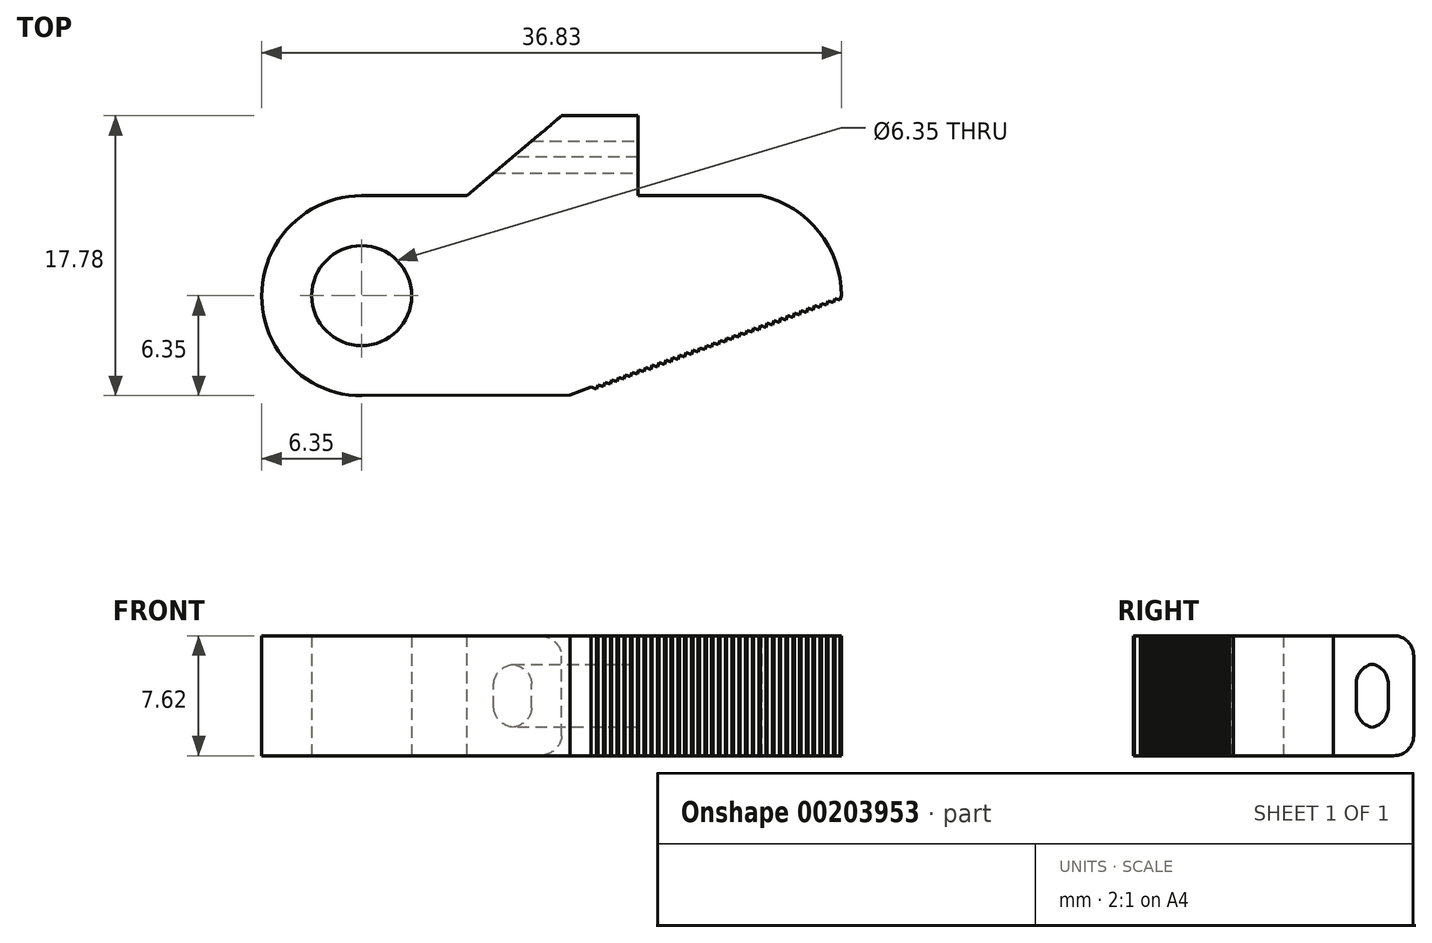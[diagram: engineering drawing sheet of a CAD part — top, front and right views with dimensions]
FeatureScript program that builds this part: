
annotation { "Feature Type Name" : "Feature", "Feature Type Description" : "" }
export const myFeature = defineFeature(function(context is Context, id is Id, definition is map)
    precondition{}
    {
        {
            var Q0;
            Q0=qCreatedBy(makeId("Top.planeOp"),FACE);
            var sketch = newSketch(context, id + "F0", { "sketchPlane" : qUnion([Q0])});
            skCircle(sketch, "E0", {"center": v(0, 0) * mm, "radius": 3.18 * mm});
            skCircle(sketch, "E1", {"center": v(0, 0) * mm, "radius": 6.35 * mm});
            skLineSegment(sketch, "E2", {"start": v(0, 0) * mm, "end": v(30.48, 0) * mm});
            skLineSegment(sketch, "E3", {"start": v(0, 0) * mm, "end": v(25.4, 0) * mm});
            skLineSegment(sketch, "E4", {"start": v(25.4, 0) * mm, "end": v(25.4, 6.35) * mm});
            skLineSegment(sketch, "E5", {"start": v(25.4, 0) * mm, "end": v(25.4, -6.35) * mm});
            skArc(sketch, "E6", {"start": v(30.48, 0) * mm, "mid": v(29.04, 4.06) * mm, "end": v(25.4, 6.35) * mm});
            skLineSegment(sketch, "E7", {"start": v(30.48, 0) * mm, "end": v(13.24, -6.3) * mm});
            skLineSegment(sketch, "E8", {"start": v(13.24, -6.3) * mm, "end": v(0, -6.35) * mm});
            skLineSegment(sketch, "E9", {"start": v(25.4, 6.35) * mm, "end": v(0, 6.35) * mm});
            skLineSegment(sketch, "E10", {"start": v(30.48, 0) * mm, "end": v(30.39, -0.28) * mm});
            skLineSegment(sketch, "E11", {"start": v(30.39, -0.28) * mm, "end": v(30.03, -0.16) * mm});
            skLineSegment(sketch, "E12.1.0.0", {"start": v(29.96, -0.44) * mm, "end": v(29.6, -0.32) * mm});
            skLineSegment(sketch, "E12.1.0.1", {"start": v(30.05, -0.16) * mm, "end": v(29.96, -0.44) * mm});
            skLineSegment(sketch, "E12.2.0.0", {"start": v(29.53, -0.6) * mm, "end": v(29.18, -0.48) * mm});
            skLineSegment(sketch, "E12.2.0.1", {"start": v(29.62, -0.31) * mm, "end": v(29.53, -0.6) * mm});
            skLineSegment(sketch, "E12.3.0.0", {"start": v(29.1, -0.75) * mm, "end": v(28.75, -0.63) * mm});
            skLineSegment(sketch, "E12.3.0.1", {"start": v(29.2, -0.47) * mm, "end": v(29.1, -0.75) * mm});
            skLineSegment(sketch, "E12.4.0.0", {"start": v(28.67, -0.9) * mm, "end": v(28.32, -0.8) * mm});
            skLineSegment(sketch, "E12.4.0.1", {"start": v(28.76, -0.63) * mm, "end": v(28.67, -0.9) * mm});
            skLineSegment(sketch, "E12.5.0.0", {"start": v(28.24, -1.06) * mm, "end": v(27.89, -0.95) * mm});
            skLineSegment(sketch, "E12.5.0.1", {"start": v(28.33, -0.79) * mm, "end": v(28.24, -1.06) * mm});
            skLineSegment(sketch, "E12.6.0.0", {"start": v(27.81, -1.22) * mm, "end": v(27.46, -1.1) * mm});
            skLineSegment(sketch, "E12.6.0.1", {"start": v(27.9, -0.94) * mm, "end": v(27.81, -1.22) * mm});
            skLineSegment(sketch, "E12.7.0.0", {"start": v(27.38, -1.38) * mm, "end": v(27.03, -1.26) * mm});
            skLineSegment(sketch, "E12.7.0.1", {"start": v(27.47, -1.1) * mm, "end": v(27.38, -1.38) * mm});
            skLineSegment(sketch, "E12.8.0.0", {"start": v(26.95, -1.54) * mm, "end": v(26.6, -1.42) * mm});
            skLineSegment(sketch, "E12.8.0.1", {"start": v(27.05, -1.26) * mm, "end": v(26.95, -1.54) * mm});
            skLineSegment(sketch, "E12.9.0.0", {"start": v(26.53, -1.7) * mm, "end": v(26.17, -1.58) * mm});
            skLineSegment(sketch, "E12.9.0.1", {"start": v(26.62, -1.41) * mm, "end": v(26.53, -1.7) * mm});
            skLineSegment(sketch, "E12.direction1", {"start": v(30.03, -0.16) * mm, "end": v(29.6, -0.32) * mm, "construction": true});
            skLineSegment(sketch, "E13.1.0.0", {"start": v(26.1, -1.85) * mm, "end": v(25.74, -1.73) * mm});
            skLineSegment(sketch, "E13.1.0.1", {"start": v(26.19, -1.57) * mm, "end": v(26.1, -1.85) * mm});
            skLineSegment(sketch, "E13.2.0.0", {"start": v(25.67, -2) * mm, "end": v(25.31, -1.9) * mm});
            skLineSegment(sketch, "E13.2.0.1", {"start": v(25.76, -1.73) * mm, "end": v(25.67, -2) * mm});
            skLineSegment(sketch, "E13.3.0.0", {"start": v(25.24, -2.16) * mm, "end": v(24.88, -2.05) * mm});
            skLineSegment(sketch, "E13.3.0.1", {"start": v(25.33, -1.88) * mm, "end": v(25.24, -2.16) * mm});
            skLineSegment(sketch, "E13.4.0.0", {"start": v(24.8, -2.32) * mm, "end": v(24.45, -2.2) * mm});
            skLineSegment(sketch, "E13.4.0.1", {"start": v(24.9, -2.04) * mm, "end": v(24.8, -2.32) * mm});
            skLineSegment(sketch, "E13.5.0.0", {"start": v(24.38, -2.48) * mm, "end": v(24.02, -2.36) * mm});
            skLineSegment(sketch, "E13.5.0.1", {"start": v(24.47, -2.2) * mm, "end": v(24.38, -2.48) * mm});
            skLineSegment(sketch, "E13.6.0.0", {"start": v(23.95, -2.63) * mm, "end": v(23.6, -2.52) * mm});
            skLineSegment(sketch, "E13.6.0.1", {"start": v(24.04, -2.36) * mm, "end": v(23.95, -2.63) * mm});
            skLineSegment(sketch, "E13.7.0.0", {"start": v(23.52, -2.8) * mm, "end": v(23.16, -2.67) * mm});
            skLineSegment(sketch, "E13.7.0.1", {"start": v(23.6, -2.51) * mm, "end": v(23.52, -2.8) * mm});
            skLineSegment(sketch, "E13.8.0.0", {"start": v(23.09, -2.95) * mm, "end": v(22.73, -2.83) * mm});
            skLineSegment(sketch, "E13.8.0.1", {"start": v(23.18, -2.67) * mm, "end": v(23.09, -2.95) * mm});
            skLineSegment(sketch, "E13.9.0.0", {"start": v(22.66, -3.1) * mm, "end": v(22.3, -2.99) * mm});
            skLineSegment(sketch, "E13.9.0.1", {"start": v(22.75, -2.83) * mm, "end": v(22.66, -3.1) * mm});
            skLineSegment(sketch, "E13.direction1", {"start": v(26.17, -1.58) * mm, "end": v(25.74, -1.73) * mm, "construction": true});
            skLineSegment(sketch, "E14.1.0.0", {"start": v(22.23, -3.26) * mm, "end": v(21.88, -3.15) * mm});
            skLineSegment(sketch, "E14.1.0.1", {"start": v(22.32, -2.98) * mm, "end": v(22.23, -3.26) * mm});
            skLineSegment(sketch, "E14.2.0.0", {"start": v(21.8, -3.42) * mm, "end": v(21.45, -3.3) * mm});
            skLineSegment(sketch, "E14.2.0.1", {"start": v(21.9, -3.14) * mm, "end": v(21.8, -3.42) * mm});
            skLineSegment(sketch, "E14.3.0.0", {"start": v(21.37, -3.57) * mm, "end": v(21.02, -3.46) * mm});
            skLineSegment(sketch, "E14.3.0.1", {"start": v(21.46, -3.3) * mm, "end": v(21.37, -3.57) * mm});
            skLineSegment(sketch, "E14.4.0.0", {"start": v(20.94, -3.73) * mm, "end": v(20.59, -3.62) * mm});
            skLineSegment(sketch, "E14.4.0.1", {"start": v(21.03, -3.45) * mm, "end": v(20.94, -3.73) * mm});
            skLineSegment(sketch, "E14.5.0.0", {"start": v(20.51, -3.89) * mm, "end": v(20.16, -3.77) * mm});
            skLineSegment(sketch, "E14.5.0.1", {"start": v(20.6, -3.61) * mm, "end": v(20.51, -3.89) * mm});
            skLineSegment(sketch, "E14.6.0.0", {"start": v(20.08, -4.05) * mm, "end": v(19.73, -3.93) * mm});
            skLineSegment(sketch, "E14.6.0.1", {"start": v(20.17, -3.77) * mm, "end": v(20.08, -4.05) * mm});
            skLineSegment(sketch, "E14.7.0.0", {"start": v(19.65, -4.2) * mm, "end": v(19.3, -4.09) * mm});
            skLineSegment(sketch, "E14.7.0.1", {"start": v(19.74, -3.92) * mm, "end": v(19.65, -4.2) * mm});
            skLineSegment(sketch, "E14.8.0.0", {"start": v(19.22, -4.36) * mm, "end": v(18.87, -4.24) * mm});
            skLineSegment(sketch, "E14.8.0.1", {"start": v(19.32, -4.08) * mm, "end": v(19.22, -4.36) * mm});
            skLineSegment(sketch, "E14.9.0.0", {"start": v(18.8, -4.52) * mm, "end": v(18.44, -4.4) * mm});
            skLineSegment(sketch, "E14.9.0.1", {"start": v(18.89, -4.24) * mm, "end": v(18.8, -4.52) * mm});
            skLineSegment(sketch, "E14.direction1", {"start": v(22.3, -2.99) * mm, "end": v(21.88, -3.15) * mm, "construction": true});
            skLineSegment(sketch, "E15.1.0.0", {"start": v(18.46, -4.4) * mm, "end": v(18.37, -4.67) * mm});
            skLineSegment(sketch, "E15.1.0.1", {"start": v(18.37, -4.67) * mm, "end": v(18.01, -4.56) * mm});
            skLineSegment(sketch, "E15.2.0.0", {"start": v(18.03, -4.55) * mm, "end": v(17.94, -4.83) * mm});
            skLineSegment(sketch, "E15.2.0.1", {"start": v(17.94, -4.83) * mm, "end": v(17.58, -4.71) * mm});
            skLineSegment(sketch, "E15.3.0.0", {"start": v(17.6, -4.7) * mm, "end": v(17.5, -4.99) * mm});
            skLineSegment(sketch, "E15.3.0.1", {"start": v(17.5, -4.99) * mm, "end": v(17.15, -4.87) * mm});
            skLineSegment(sketch, "E15.4.0.0", {"start": v(17.17, -4.86) * mm, "end": v(17.08, -5.14) * mm});
            skLineSegment(sketch, "E15.4.0.1", {"start": v(17.08, -5.14) * mm, "end": v(16.72, -5.03) * mm});
            skLineSegment(sketch, "E15.5.0.0", {"start": v(16.74, -5.02) * mm, "end": v(16.65, -5.3) * mm});
            skLineSegment(sketch, "E15.5.0.1", {"start": v(16.65, -5.3) * mm, "end": v(16.3, -5.18) * mm});
            skLineSegment(sketch, "E15.6.0.0", {"start": v(16.3, -5.18) * mm, "end": v(16.22, -5.45) * mm});
            skLineSegment(sketch, "E15.6.0.1", {"start": v(16.22, -5.45) * mm, "end": v(15.86, -5.34) * mm});
            skLineSegment(sketch, "E15.7.0.0", {"start": v(15.88, -5.33) * mm, "end": v(15.79, -5.61) * mm});
            skLineSegment(sketch, "E15.7.0.1", {"start": v(15.79, -5.61) * mm, "end": v(15.43, -5.5) * mm});
            skLineSegment(sketch, "E15.8.0.0", {"start": v(15.45, -5.49) * mm, "end": v(15.36, -5.77) * mm});
            skLineSegment(sketch, "E15.8.0.1", {"start": v(15.36, -5.77) * mm, "end": v(15, -5.65) * mm});
            skLineSegment(sketch, "E15.9.0.0", {"start": v(15.02, -5.65) * mm, "end": v(14.93, -5.92) * mm});
            skLineSegment(sketch, "E15.9.0.1", {"start": v(14.93, -5.92) * mm, "end": v(14.57, -5.8) * mm});
            skLineSegment(sketch, "E15.direction1", {"start": v(18.8, -4.52) * mm, "end": v(18.37, -4.67) * mm, "construction": true});
            skLineSegment(sketch, "E16", {"start": v(14.57, -5.8) * mm, "end": v(29.04, 0.72) * mm});
            skLineSegment(sketch, "E17", {"start": v(29.04, 0.72) * mm, "end": v(30.48, 0) * mm});
            skSolve(sketch);
        }
        {
            var Q0;
            Q0 = qSketchRegion(id + "F0", true);
            var Q1;
            {var subQ1=sQuery(id+"F0.wireOp",EDGE,"E2");var subQ3=sQuery(id+"F0.wireOp",EDGE,"E16");var subQ4=makeQuery(id+"F0.imprint","INTERSECT",VERTEX,{"derivedFrom":[subQ1,subQ3]});Q1=makeQuery(id+"F0.imprint","IMPRINT",FACE,{"disambiguationData":[TD([[makeQuery(id+"F0.imprint","IMPRINT",EDGE,{"disambiguationData":[TD([[subQ4,1.0]])],"derivedFrom":subQ3}),1.0]])]});}
            extrude(context, id + "F1", {"entities" : qUnion([Q0, Q1]), "depth" : 7.62 * mm});
        }
        {
            var Q0;
            Q0=makeQuery(id+"F1.opExtrude","CAP_FACE",FACE,{"disambiguationData":[OSD([sQuery(id+"F0.wireOp",EDGE,"E0"),sQuery(id+"F0.wireOp",EDGE,"E1"),sQuery(id+"F0.wireOp",EDGE,"E6"),sQuery(id+"F0.wireOp",EDGE,"E7"),sQuery(id+"F0.wireOp",EDGE,"E8"),sQuery(id+"F0.wireOp",EDGE,"E9"),sQuery(id+"F0.wireOp",EDGE,"E10"),sQuery(id+"F0.wireOp",EDGE,"E11"),sQuery(id+"F0.wireOp",EDGE,"E12.1.0.0"),sQuery(id+"F0.wireOp",EDGE,"E12.1.0.1"),sQuery(id+"F0.wireOp",EDGE,"E12.2.0.0"),sQuery(id+"F0.wireOp",EDGE,"E12.2.0.1"),sQuery(id+"F0.wireOp",EDGE,"E12.3.0.0"),sQuery(id+"F0.wireOp",EDGE,"E12.3.0.1"),sQuery(id+"F0.wireOp",EDGE,"E12.4.0.0"),sQuery(id+"F0.wireOp",EDGE,"E12.4.0.1"),sQuery(id+"F0.wireOp",EDGE,"E12.5.0.0"),sQuery(id+"F0.wireOp",EDGE,"E12.5.0.1"),sQuery(id+"F0.wireOp",EDGE,"E12.6.0.0"),sQuery(id+"F0.wireOp",EDGE,"E12.6.0.1"),sQuery(id+"F0.wireOp",EDGE,"E12.7.0.0"),sQuery(id+"F0.wireOp",EDGE,"E12.7.0.1"),sQuery(id+"F0.wireOp",EDGE,"E12.8.0.0"),sQuery(id+"F0.wireOp",EDGE,"E12.8.0.1"),sQuery(id+"F0.wireOp",EDGE,"E12.9.0.0"),sQuery(id+"F0.wireOp",EDGE,"E12.9.0.1"),sQuery(id+"F0.wireOp",EDGE,"E13.1.0.0"),sQuery(id+"F0.wireOp",EDGE,"E13.1.0.1"),sQuery(id+"F0.wireOp",EDGE,"E13.2.0.0"),sQuery(id+"F0.wireOp",EDGE,"E13.2.0.1"),sQuery(id+"F0.wireOp",EDGE,"E13.3.0.0"),sQuery(id+"F0.wireOp",EDGE,"E13.3.0.1"),sQuery(id+"F0.wireOp",EDGE,"E13.4.0.0"),sQuery(id+"F0.wireOp",EDGE,"E13.4.0.1"),sQuery(id+"F0.wireOp",EDGE,"E13.5.0.0"),sQuery(id+"F0.wireOp",EDGE,"E13.5.0.1"),sQuery(id+"F0.wireOp",EDGE,"E13.6.0.0"),sQuery(id+"F0.wireOp",EDGE,"E13.6.0.1"),sQuery(id+"F0.wireOp",EDGE,"E13.7.0.0"),sQuery(id+"F0.wireOp",EDGE,"E13.7.0.1"),sQuery(id+"F0.wireOp",EDGE,"E13.8.0.0"),sQuery(id+"F0.wireOp",EDGE,"E13.8.0.1"),sQuery(id+"F0.wireOp",EDGE,"E13.9.0.0"),sQuery(id+"F0.wireOp",EDGE,"E13.9.0.1"),sQuery(id+"F0.wireOp",EDGE,"E14.1.0.0"),sQuery(id+"F0.wireOp",EDGE,"E14.1.0.1"),sQuery(id+"F0.wireOp",EDGE,"E14.2.0.0"),sQuery(id+"F0.wireOp",EDGE,"E14.2.0.1"),sQuery(id+"F0.wireOp",EDGE,"E14.3.0.0"),sQuery(id+"F0.wireOp",EDGE,"E14.3.0.1"),sQuery(id+"F0.wireOp",EDGE,"E14.4.0.0"),sQuery(id+"F0.wireOp",EDGE,"E14.4.0.1"),sQuery(id+"F0.wireOp",EDGE,"E14.5.0.0"),sQuery(id+"F0.wireOp",EDGE,"E14.5.0.1"),sQuery(id+"F0.wireOp",EDGE,"E14.6.0.0"),sQuery(id+"F0.wireOp",EDGE,"E14.6.0.1"),sQuery(id+"F0.wireOp",EDGE,"E14.7.0.0"),sQuery(id+"F0.wireOp",EDGE,"E14.7.0.1"),sQuery(id+"F0.wireOp",EDGE,"E14.8.0.0"),sQuery(id+"F0.wireOp",EDGE,"E14.8.0.1"),sQuery(id+"F0.wireOp",EDGE,"E14.9.0.0"),sQuery(id+"F0.wireOp",EDGE,"E14.9.0.1"),sQuery(id+"F0.wireOp",EDGE,"E15.1.0.0"),sQuery(id+"F0.wireOp",EDGE,"E15.1.0.1"),sQuery(id+"F0.wireOp",EDGE,"E15.2.0.0"),sQuery(id+"F0.wireOp",EDGE,"E15.2.0.1"),sQuery(id+"F0.wireOp",EDGE,"E15.3.0.0"),sQuery(id+"F0.wireOp",EDGE,"E15.3.0.1"),sQuery(id+"F0.wireOp",EDGE,"E15.4.0.0"),sQuery(id+"F0.wireOp",EDGE,"E15.4.0.1"),sQuery(id+"F0.wireOp",EDGE,"E15.5.0.0"),sQuery(id+"F0.wireOp",EDGE,"E15.5.0.1"),sQuery(id+"F0.wireOp",EDGE,"E15.6.0.0"),sQuery(id+"F0.wireOp",EDGE,"E15.6.0.1"),sQuery(id+"F0.wireOp",EDGE,"E15.7.0.0"),sQuery(id+"F0.wireOp",EDGE,"E15.7.0.1"),sQuery(id+"F0.wireOp",EDGE,"E15.8.0.0"),sQuery(id+"F0.wireOp",EDGE,"E15.8.0.1"),sQuery(id+"F0.wireOp",EDGE,"E15.9.0.0"),sQuery(id+"F0.wireOp",EDGE,"E15.9.0.1")])],"isStart":false});
            var sketch = newSketch(context, id + "F2", { "sketchPlane" : qUnion([Q0])});
            skLineSegment(sketch, "E18.bottom", {"start": v(12.7, 6.35) * mm, "end": v(21.59, 6.35) * mm});
            skLineSegment(sketch, "E18.top", {"start": v(12.7, 11.43) * mm, "end": v(21.59, 11.43) * mm});
            skLineSegment(sketch, "E18.left", {"start": v(12.7, 6.35) * mm, "end": v(12.7, 11.43) * mm});
            skLineSegment(sketch, "E18.right", {"start": v(21.59, 6.35) * mm, "end": v(21.59, 11.43) * mm});
            skLineSegment(sketch, "E19", {"start": v(12.7, 11.43) * mm, "end": v(6.69, 6.35) * mm});
            skLineSegment(sketch, "E20", {"start": v(6.69, 6.35) * mm, "end": v(12.7, 6.35) * mm});
            skSolve(sketch);
        }
        {
            var Q0;
            Q0 = qSketchRegion(id + "F2", true);
            extrude(context, id + "F3", {"entities" : qUnion([Q0]), "operationType" : NewBodyOperationType.ADD, "oppositeDirection" : true, "depth" : 7.62 * mm});
        }
        {
            var Q0;
            Q0=makeQuery(id+"F3.opExtrude","SWEPT_FACE",FACE,{"disambiguationData":[OSD([sQuery(id+"F2.wireOp",EDGE,"E18.right")])]});
            var sketch = newSketch(context, id + "F4", { "sketchPlane" : qUnion([Q0])});
            skLineSegment(sketch, "E21", {"start": v(6.35, 3.81) * mm, "end": v(7.79, 3.81) * mm});
            skLineSegment(sketch, "E22.bottom", {"start": v(7.79, 3.81) * mm, "end": v(9.82, 3.81) * mm});
            skLineSegment(sketch, "E22.top", {"start": v(7.79, 1.78) * mm, "end": v(9.82, 1.78) * mm});
            skLineSegment(sketch, "E22.left", {"start": v(7.79, 3.81) * mm, "end": v(7.79, 1.78) * mm});
            skLineSegment(sketch, "E22.right", {"start": v(9.82, 3.81) * mm, "end": v(9.82, 1.78) * mm});
            skLineSegment(sketch, "E23.top", {"start": v(7.79, 5.84) * mm, "end": v(9.82, 5.84) * mm});
            skLineSegment(sketch, "E23.left", {"start": v(7.79, 3.8) * mm, "end": v(7.79, 5.84) * mm});
            skLineSegment(sketch, "E23.right", {"start": v(9.82, 3.81) * mm, "end": v(9.82, 5.84) * mm});
            skSolve(sketch);
        }
        {
            var Q0;
            Q0=makeQuery(id+"F4.imprint","IMPRINT",FACE,{"disambiguationData":[TD([[makeQuery(id+"F4.imprint","IMPRINT",EDGE,{"derivedFrom":sQuery(id+"F4.wireOp",EDGE,"E22.top")}),1.0]])]});
            var Q1;
            Q1=makeQuery(id+"F4.imprint","IMPRINT",FACE,{"disambiguationData":[TD([[makeQuery(id+"F4.imprint","IMPRINT",EDGE,{"derivedFrom":sQuery(id+"F4.wireOp",EDGE,"E22.bottom")}),1.0]])]});
            extrude(context, id + "F5", {"entities" : qUnion([Q0, Q1]), "operationType" : NewBodyOperationType.REMOVE, "oppositeDirection" : true, "depth" : 25.4 * mm});
        }
        {
            var Q0;
            Q0=makeQuery(id+"F3.opExtrude","CAP_EDGE",EDGE,{"disambiguationData":[OSD([sQuery(id+"F2.wireOp",EDGE,"E18.top")])],"isStart":false});
            var Q1;
            Q1=makeQuery(id+"F3.opExtrude","CAP_EDGE",EDGE,{"disambiguationData":[OSD([sQuery(id+"F2.wireOp",EDGE,"E18.top")])],"isStart":true});
            var Q2;
            Q2=makeQuery(id+"F5.boolean.opBoolean","COPY",EDGE,{"derivedFrom":makeQuery(id+"F5.opExtrude","SWEPT_EDGE",EDGE,{"disambiguationData":[OSD([sQuery(id+"F4.wireOp",EDGE,"E23.top"),sQuery(id+"F4.wireOp",EDGE,"E23.left")])]})});
            var Q3;
            Q3=makeQuery(id+"F5.boolean.opBoolean","COPY",EDGE,{"derivedFrom":makeQuery(id+"F5.opExtrude","SWEPT_EDGE",EDGE,{"disambiguationData":[OSD([sQuery(id+"F4.wireOp",EDGE,"E23.top"),sQuery(id+"F4.wireOp",EDGE,"E23.right")])]})});
            var Q4;
            Q4=makeQuery(id+"F5.boolean.opBoolean","COPY",EDGE,{"derivedFrom":makeQuery(id+"F5.opExtrude","SWEPT_EDGE",EDGE,{"disambiguationData":[OSD([sQuery(id+"F4.wireOp",EDGE,"E22.top"),sQuery(id+"F4.wireOp",EDGE,"E22.left")])]})});
            var Q5;
            Q5=makeQuery(id+"F5.boolean.opBoolean","COPY",EDGE,{"derivedFrom":makeQuery(id+"F5.opExtrude","SWEPT_EDGE",EDGE,{"disambiguationData":[OSD([sQuery(id+"F4.wireOp",EDGE,"E22.top"),sQuery(id+"F4.wireOp",EDGE,"E22.right")])]})});
            fillet(context, id + "F6", {"entities" : qUnion([Q0, Q1, Q2, Q3, Q4, Q5]), "radius" : 1.27 * mm, "tangentPropagation" : true, "allowEdgeOverflow" : false});
        }
        {
            var Q0;
            Q0=makeQuery(id+"F3.boolean.opBoolean","MERGE",FACE,{"derivedFrom":[makeQuery(id+"F1.opExtrude","CAP_FACE",FACE,{"disambiguationData":[OSD([sQuery(id+"F0.wireOp",EDGE,"E0"),sQuery(id+"F0.wireOp",EDGE,"E1"),sQuery(id+"F0.wireOp",EDGE,"E6"),sQuery(id+"F0.wireOp",EDGE,"E7"),sQuery(id+"F0.wireOp",EDGE,"E8"),sQuery(id+"F0.wireOp",EDGE,"E9"),sQuery(id+"F0.wireOp",EDGE,"E10"),sQuery(id+"F0.wireOp",EDGE,"E11"),sQuery(id+"F0.wireOp",EDGE,"E12.1.0.0"),sQuery(id+"F0.wireOp",EDGE,"E12.1.0.1"),sQuery(id+"F0.wireOp",EDGE,"E12.2.0.0"),sQuery(id+"F0.wireOp",EDGE,"E12.2.0.1"),sQuery(id+"F0.wireOp",EDGE,"E12.3.0.0"),sQuery(id+"F0.wireOp",EDGE,"E12.3.0.1"),sQuery(id+"F0.wireOp",EDGE,"E12.4.0.0"),sQuery(id+"F0.wireOp",EDGE,"E12.4.0.1"),sQuery(id+"F0.wireOp",EDGE,"E12.5.0.0"),sQuery(id+"F0.wireOp",EDGE,"E12.5.0.1"),sQuery(id+"F0.wireOp",EDGE,"E12.6.0.0"),sQuery(id+"F0.wireOp",EDGE,"E12.6.0.1"),sQuery(id+"F0.wireOp",EDGE,"E12.7.0.0"),sQuery(id+"F0.wireOp",EDGE,"E12.7.0.1"),sQuery(id+"F0.wireOp",EDGE,"E12.8.0.0"),sQuery(id+"F0.wireOp",EDGE,"E12.8.0.1"),sQuery(id+"F0.wireOp",EDGE,"E12.9.0.0"),sQuery(id+"F0.wireOp",EDGE,"E12.9.0.1"),sQuery(id+"F0.wireOp",EDGE,"E13.1.0.0"),sQuery(id+"F0.wireOp",EDGE,"E13.1.0.1"),sQuery(id+"F0.wireOp",EDGE,"E13.2.0.0"),sQuery(id+"F0.wireOp",EDGE,"E13.2.0.1"),sQuery(id+"F0.wireOp",EDGE,"E13.3.0.0"),sQuery(id+"F0.wireOp",EDGE,"E13.3.0.1"),sQuery(id+"F0.wireOp",EDGE,"E13.4.0.0"),sQuery(id+"F0.wireOp",EDGE,"E13.4.0.1"),sQuery(id+"F0.wireOp",EDGE,"E13.5.0.0"),sQuery(id+"F0.wireOp",EDGE,"E13.5.0.1"),sQuery(id+"F0.wireOp",EDGE,"E13.6.0.0"),sQuery(id+"F0.wireOp",EDGE,"E13.6.0.1"),sQuery(id+"F0.wireOp",EDGE,"E13.7.0.0"),sQuery(id+"F0.wireOp",EDGE,"E13.7.0.1"),sQuery(id+"F0.wireOp",EDGE,"E13.8.0.0"),sQuery(id+"F0.wireOp",EDGE,"E13.8.0.1"),sQuery(id+"F0.wireOp",EDGE,"E13.9.0.0"),sQuery(id+"F0.wireOp",EDGE,"E13.9.0.1"),sQuery(id+"F0.wireOp",EDGE,"E14.1.0.0"),sQuery(id+"F0.wireOp",EDGE,"E14.1.0.1"),sQuery(id+"F0.wireOp",EDGE,"E14.2.0.0"),sQuery(id+"F0.wireOp",EDGE,"E14.2.0.1"),sQuery(id+"F0.wireOp",EDGE,"E14.3.0.0"),sQuery(id+"F0.wireOp",EDGE,"E14.3.0.1"),sQuery(id+"F0.wireOp",EDGE,"E14.4.0.0"),sQuery(id+"F0.wireOp",EDGE,"E14.4.0.1"),sQuery(id+"F0.wireOp",EDGE,"E14.5.0.0"),sQuery(id+"F0.wireOp",EDGE,"E14.5.0.1"),sQuery(id+"F0.wireOp",EDGE,"E14.6.0.0"),sQuery(id+"F0.wireOp",EDGE,"E14.6.0.1"),sQuery(id+"F0.wireOp",EDGE,"E14.7.0.0"),sQuery(id+"F0.wireOp",EDGE,"E14.7.0.1"),sQuery(id+"F0.wireOp",EDGE,"E14.8.0.0"),sQuery(id+"F0.wireOp",EDGE,"E14.8.0.1"),sQuery(id+"F0.wireOp",EDGE,"E14.9.0.0"),sQuery(id+"F0.wireOp",EDGE,"E14.9.0.1"),sQuery(id+"F0.wireOp",EDGE,"E15.1.0.0"),sQuery(id+"F0.wireOp",EDGE,"E15.1.0.1"),sQuery(id+"F0.wireOp",EDGE,"E15.2.0.0"),sQuery(id+"F0.wireOp",EDGE,"E15.2.0.1"),sQuery(id+"F0.wireOp",EDGE,"E15.3.0.0"),sQuery(id+"F0.wireOp",EDGE,"E15.3.0.1"),sQuery(id+"F0.wireOp",EDGE,"E15.4.0.0"),sQuery(id+"F0.wireOp",EDGE,"E15.4.0.1"),sQuery(id+"F0.wireOp",EDGE,"E15.5.0.0"),sQuery(id+"F0.wireOp",EDGE,"E15.5.0.1"),sQuery(id+"F0.wireOp",EDGE,"E15.6.0.0"),sQuery(id+"F0.wireOp",EDGE,"E15.6.0.1"),sQuery(id+"F0.wireOp",EDGE,"E15.7.0.0"),sQuery(id+"F0.wireOp",EDGE,"E15.7.0.1"),sQuery(id+"F0.wireOp",EDGE,"E15.8.0.0"),sQuery(id+"F0.wireOp",EDGE,"E15.8.0.1"),sQuery(id+"F0.wireOp",EDGE,"E15.9.0.0"),sQuery(id+"F0.wireOp",EDGE,"E15.9.0.1")])],"isStart":false}),makeQuery(id+"F3.opExtrude","CAP_FACE",FACE,{"disambiguationData":[OSD([sQuery(id+"F2.wireOp",EDGE,"E18.bottom"),sQuery(id+"F2.wireOp",EDGE,"E18.top"),sQuery(id+"F2.wireOp",EDGE,"E18.right"),sQuery(id+"F2.wireOp",EDGE,"E19"),sQuery(id+"F2.wireOp",EDGE,"E20")])],"isStart":true})]});
            var sketch = newSketch(context, id + "F7", { "sketchPlane" : qUnion([Q0])});
            skLineSegment(sketch, "E24.bottom", {"start": v(21.59, 6.35) * mm, "end": v(17.53, 6.35) * mm});
            skLineSegment(sketch, "E24.top", {"start": v(21.59, 14.72) * mm, "end": v(17.53, 14.72) * mm});
            skLineSegment(sketch, "E24.left", {"start": v(21.59, 6.35) * mm, "end": v(21.59, 14.72) * mm});
            skLineSegment(sketch, "E24.right", {"start": v(17.53, 6.35) * mm, "end": v(17.53, 14.72) * mm});
            skSolve(sketch);
        }
        {
            var Q0;
            {var subQ0=sQuery(id+"F7.wireOp",EDGE,"E24.bottom");Q0=makeQuery(id+"F7.imprint","IMPRINT",FACE,{"disambiguationData":[TD([[makeQuery(id+"F7.imprint","IMPRINT",EDGE,{"derivedFrom":subQ0}),-1.0]])]});}
            var Q1;
            {var subQ0=sQuery(id+"F7.wireOp",EDGE,"E24.top");Q1=makeQuery(id+"F7.imprint","IMPRINT",FACE,{"disambiguationData":[TD([[makeQuery(id+"F7.imprint","IMPRINT",EDGE,{"derivedFrom":subQ0}),1.0]])]});}
            extrude(context, id + "F8", {"entities" : qUnion([Q0, Q1]), "operationType" : NewBodyOperationType.REMOVE, "oppositeDirection" : true, "depth" : 25.4 * mm});
        }
    });
